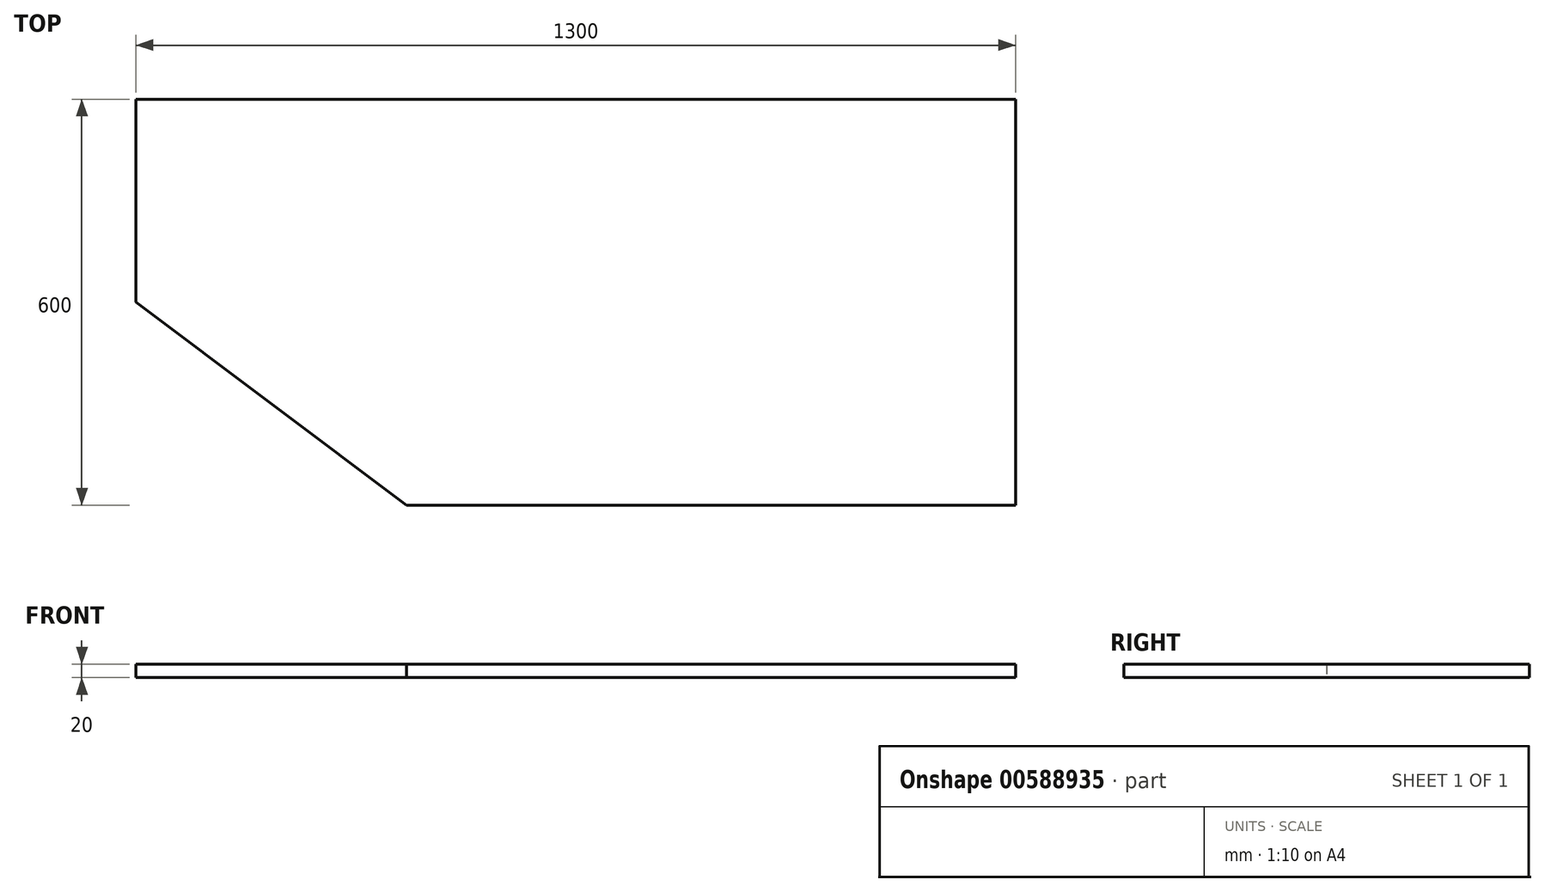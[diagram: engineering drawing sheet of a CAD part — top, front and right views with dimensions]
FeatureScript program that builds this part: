
annotation { "Feature Type Name" : "Feature", "Feature Type Description" : "" }
export const myFeature = defineFeature(function(context is Context, id is Id, definition is map)
    precondition{}
    {
        {
            var Q0;
            Q0=qCreatedBy(makeId("Top.planeOp"),FACE);
            var sketch = newSketch(context, id + "F0", { "sketchPlane" : qUnion([Q0])});
            skLineSegment(sketch, "E0.bottom", {"start": v(650, 300) * mm, "end": v(-650, 300) * mm});
            skLineSegment(sketch, "E0.left", {"start": v(650, 300) * mm, "end": v(650, -300) * mm});
            skPoint(sketch, "E0.middle", {"position": v(0, 0) * mm});
            skLineSegment(sketch, "E1", {"start": v(-650, 300) * mm, "end": v(-650, 0) * mm});
            skLineSegment(sketch, "E2", {"start": v(-650, 0) * mm, "end": v(-250, -300) * mm});
            skLineSegment(sketch, "E3", {"start": v(-250, -300) * mm, "end": v(650, -300) * mm});
            skSolve(sketch);
        }
        {
            var Q0;
            Q0=makeQuery(id+"F0.imprint","IMPRINT",FACE,{"disambiguationData":[TD([[makeQuery(id+"F0.imprint","IMPRINT",EDGE,{"derivedFrom":sQuery(id+"F0.wireOp",EDGE,"E0.bottom")}),1.0]])]});
            extrude(context, id + "F1", {"entities" : qUnion([Q0]), "depth" : 20 * mm, "offsetDistance" : 25 * mm});
        }
    });
